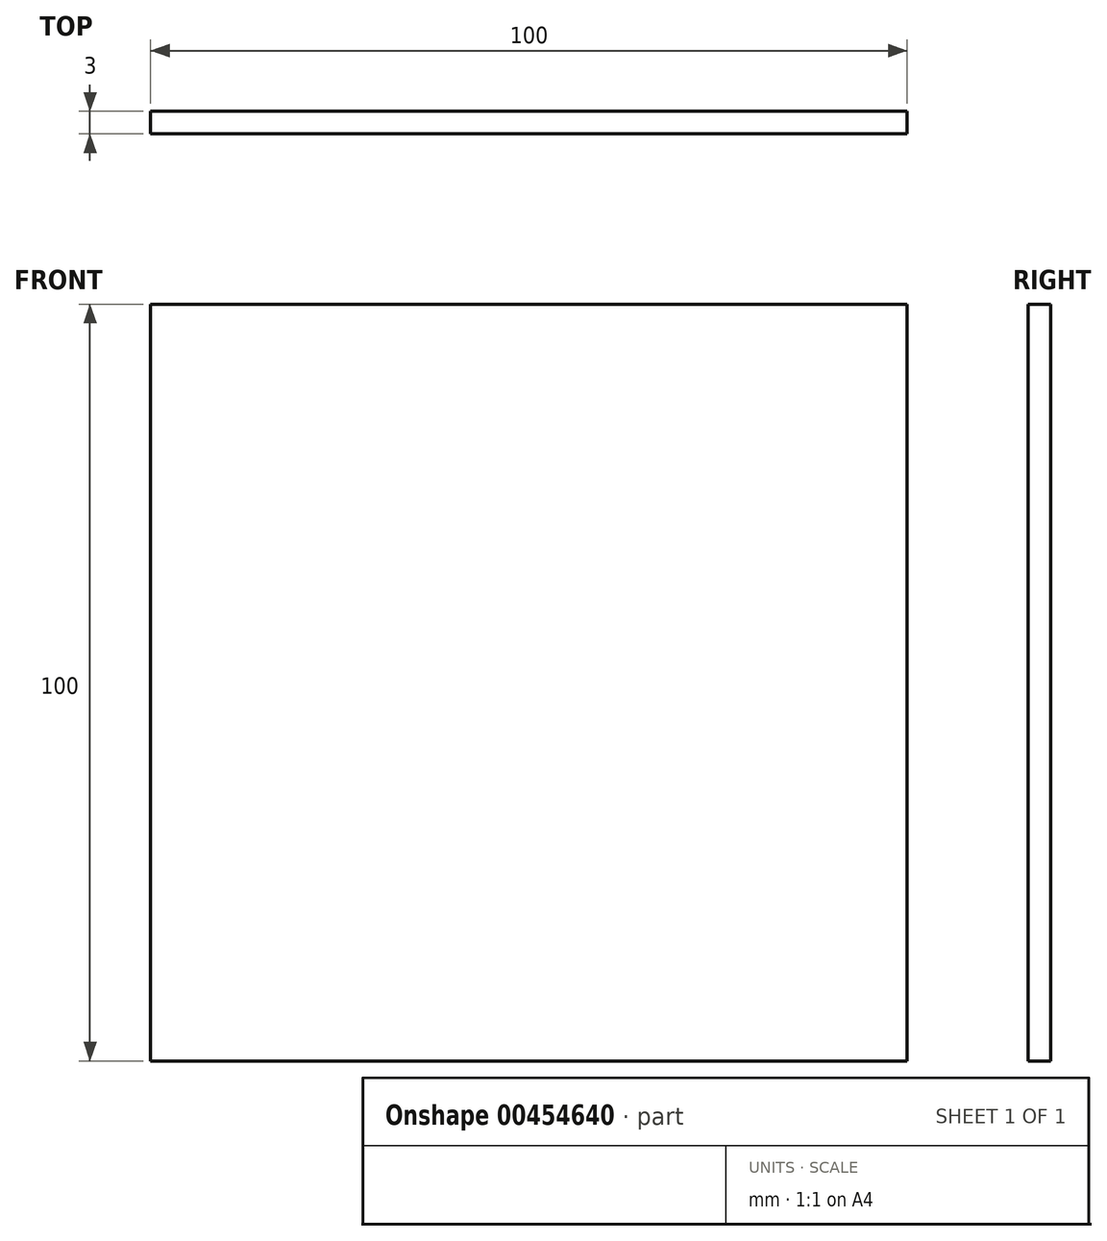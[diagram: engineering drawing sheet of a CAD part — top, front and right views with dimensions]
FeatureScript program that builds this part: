
annotation { "Feature Type Name" : "Feature", "Feature Type Description" : "" }
export const myFeature = defineFeature(function(context is Context, id is Id, definition is map)
    precondition{}
    {
        {
            var Q0;
            Q0=qCreatedBy(makeId("Front.planeOp"),FACE);
            var sketch = newSketch(context, id + "F0", { "sketchPlane" : qUnion([Q0])});
            skLineSegment(sketch, "E0.bottom", {"start": v(-41.92, 49.55) * mm, "end": v(58.08, 49.55) * mm});
            skLineSegment(sketch, "E0.top", {"start": v(-41.92, -50.45) * mm, "end": v(58.08, -50.45) * mm});
            skLineSegment(sketch, "E0.left", {"start": v(-41.92, 49.55) * mm, "end": v(-41.92, -50.45) * mm});
            skLineSegment(sketch, "E0.right", {"start": v(58.08, 49.55) * mm, "end": v(58.08, -50.45) * mm});
            skSolve(sketch);
        }
        {
            var Q0;
            Q0 = qSketchRegion(id + "F0", true);
            extrude(context, id + "F1", {"entities" : qUnion([Q0]), "depth" : 3 * mm});
        }
    });
